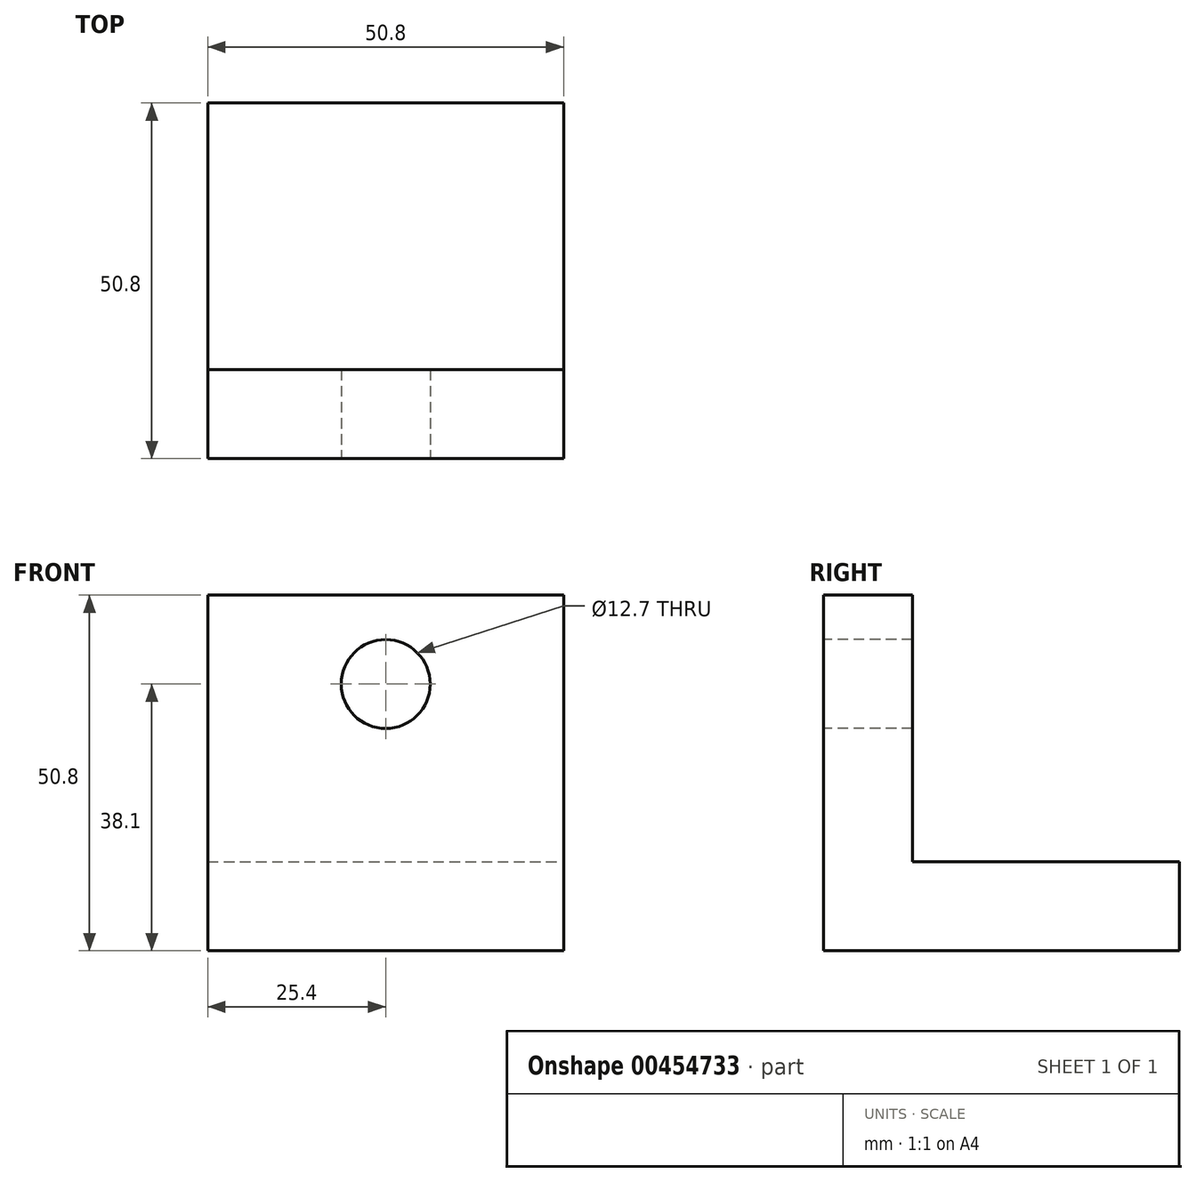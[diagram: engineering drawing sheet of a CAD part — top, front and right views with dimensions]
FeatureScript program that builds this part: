
annotation { "Feature Type Name" : "Feature", "Feature Type Description" : "" }
export const myFeature = defineFeature(function(context is Context, id is Id, definition is map)
    precondition{}
    {
        {
            var Q0;
            Q0=qCreatedBy(makeId("Top.planeOp"),FACE);
            var sketch = newSketch(context, id + "F0", { "sketchPlane" : qUnion([Q0])});
            skLineSegment(sketch, "E0.bottom", {"start": v(0, 0) * mm, "end": v(50.8, 0) * mm});
            skLineSegment(sketch, "E0.top", {"start": v(0, 50.8) * mm, "end": v(50.8, 50.8) * mm});
            skLineSegment(sketch, "E0.left", {"start": v(0, 0) * mm, "end": v(0, 50.8) * mm});
            skLineSegment(sketch, "E0.right", {"start": v(50.8, 0) * mm, "end": v(50.8, 50.8) * mm});
            skSolve(sketch);
        }
        {
            var Q0;
            Q0=makeQuery(id+"F0.imprint","IMPRINT",FACE,{"disambiguationData":[TD([[makeQuery(id+"F0.imprint","IMPRINT",EDGE,{"derivedFrom":sQuery(id+"F0.wireOp",EDGE,"E0.bottom")}),1.0]])]});
            extrude(context, id + "F1", {"entities" : qUnion([Q0]), "depth" : 12.7 * mm});
        }
        {
            var Q0;
            Q0=makeQuery(id+"F1.opExtrude","CAP_FACE",FACE,{"disambiguationData":[OSD([sQuery(id+"F0.wireOp",EDGE,"E0.bottom"),sQuery(id+"F0.wireOp",EDGE,"E0.top"),sQuery(id+"F0.wireOp",EDGE,"E0.left"),sQuery(id+"F0.wireOp",EDGE,"E0.right")])],"isStart":false});
            var sketch = newSketch(context, id + "F2", { "sketchPlane" : qUnion([Q0])});
            skLineSegment(sketch, "E1", {"start": v(0, 0) * mm, "end": v(0, 12.7) * mm});
            skLineSegment(sketch, "E2", {"start": v(0, 12.7) * mm, "end": v(50.8, 12.7) * mm});
            skSolve(sketch);
        }
        {
            var Q0;
            Q0=makeQuery(id+"F2.imprint","IMPRINT",FACE,{"disambiguationData":[TD([[makeQuery(id+"F2.imprint","IMPRINT",EDGE,{"derivedFrom":sQuery(id+"F2.wireOp",EDGE,"E1")}),-1.0]])]});
            extrude(context, id + "F3", {"entities" : qUnion([Q0]), "operationType" : NewBodyOperationType.ADD, "depth" : 38.1 * mm});
        }
        {
            var Q0;
            {var subQ0=sQuery(id+"F0.wireOp",EDGE,"E0.bottom");Q0=makeQuery(id+"F3.boolean.opBoolean","MERGE",FACE,{"derivedFrom":[makeQuery(id+"F1.opExtrude","SWEPT_FACE",FACE,{"disambiguationData":[OSD([subQ0])]}),makeQuery(id+"F3.opExtrude","SWEPT_FACE",FACE,{"disambiguationData":[OSD([subQ0])]})]});}
            var sketch = newSketch(context, id + "F4", { "sketchPlane" : qUnion([Q0])});
            skLineSegment(sketch, "E3", {"start": v(25.4, 50.8) * mm, "end": v(25.4, 38.1) * mm});
            skCircle(sketch, "E4", {"center": v(25.4, 38.1) * mm, "radius": 6.35 * mm});
            skSolve(sketch);
        }
        {
            var Q0;
            Q0=makeQuery(id+"F4.imprint","IMPRINT",FACE,{"disambiguationData":[TD([[makeQuery(id+"F4.imprint","IMPRINT",EDGE,{"derivedFrom":sQuery(id+"F4.wireOp",EDGE,"E4")}),1.0]])]});
            extrude(context, id + "F5", {"entities" : qUnion([Q0]), "operationType" : NewBodyOperationType.REMOVE, "oppositeDirection" : true, "depth" : 25.4 * mm});
        }
    });
